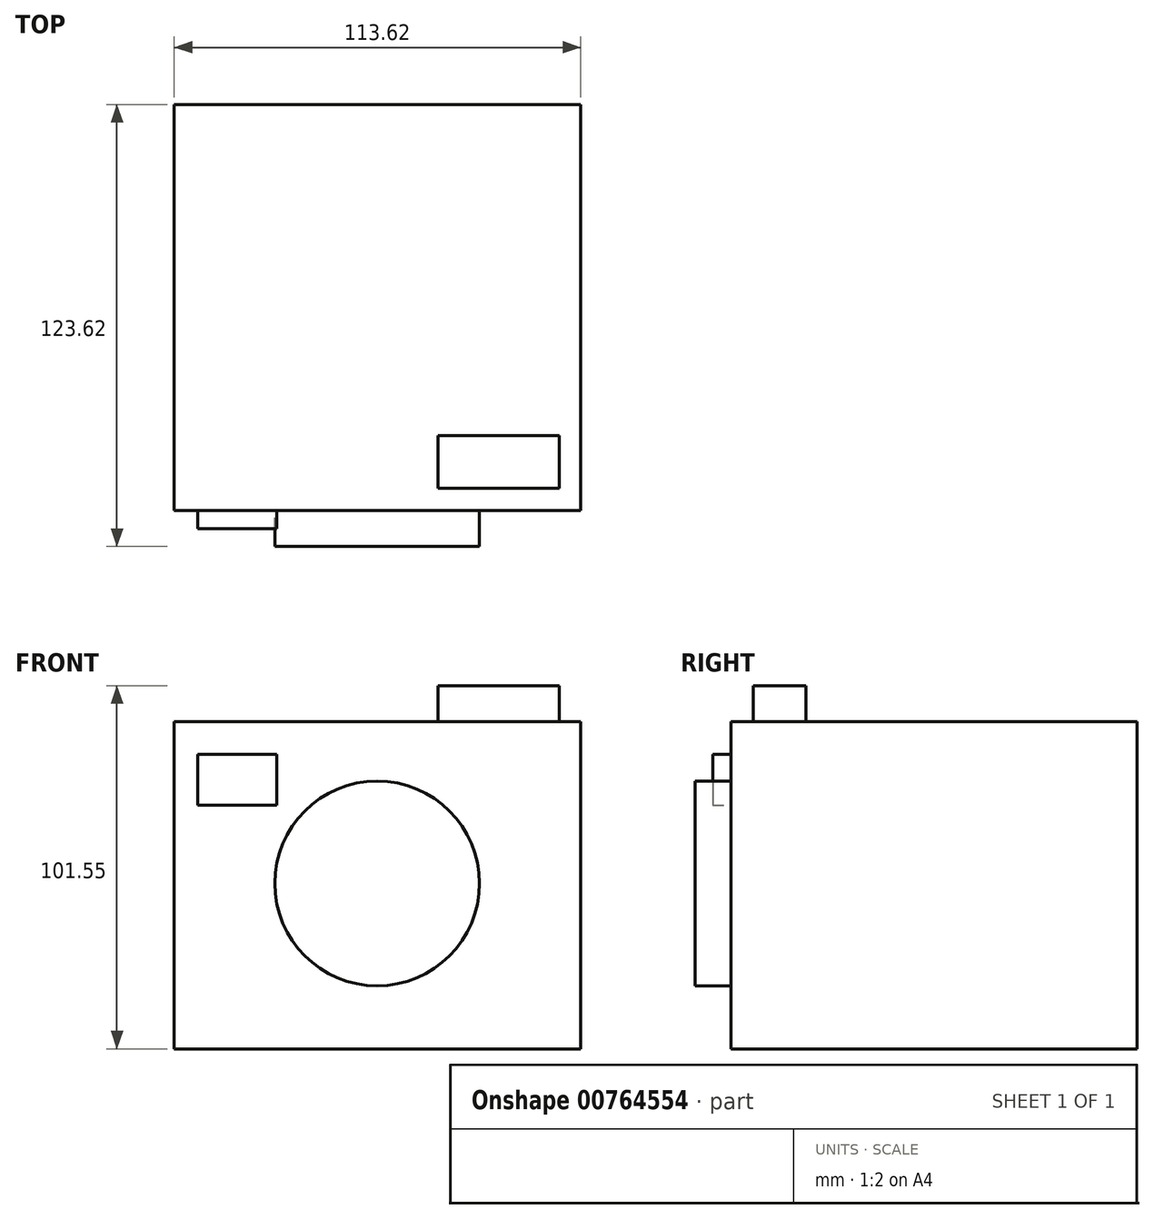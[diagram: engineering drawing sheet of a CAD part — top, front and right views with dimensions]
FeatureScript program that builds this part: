
annotation { "Feature Type Name" : "Feature", "Feature Type Description" : "" }
export const myFeature = defineFeature(function(context is Context, id is Id, definition is map)
    precondition{}
    {
        {
            var Q0;
            Q0=qCreatedBy(makeId("Front.planeOp"),FACE);
            var sketch = newSketch(context, id + "F0", { "sketchPlane" : qUnion([Q0])});
            skLineSegment(sketch, "E0.bottom", {"start": v(-56.7, 45.3) * mm, "end": v(56.91, 45.3) * mm});
            skLineSegment(sketch, "E0.top", {"start": v(-56.7, -46.26) * mm, "end": v(56.91, -46.26) * mm});
            skLineSegment(sketch, "E0.left", {"start": v(-56.7, 45.3) * mm, "end": v(-56.7, -46.26) * mm});
            skLineSegment(sketch, "E0.right", {"start": v(56.91, 45.3) * mm, "end": v(56.91, -46.26) * mm});
            skSolve(sketch);
        }
        {
            var Q0;
            Q0=makeQuery(id+"F0.imprint","IMPRINT",FACE,{"disambiguationData":[TD([[makeQuery(id+"F0.imprint","IMPRINT",EDGE,{"derivedFrom":sQuery(id+"F0.wireOp",EDGE,"E0.bottom")}),-1.0]])]});
            extrude(context, id + "F1", {"entities" : qUnion([Q0]), "depth" : 113.62 * mm, "offsetDistance" : 25.4 * mm});
        }
        {
            var Q0;
            Q0=makeQuery(id+"F1.opExtrude","CAP_FACE",FACE,{"disambiguationData":[OSD([sQuery(id+"F0.wireOp",EDGE,"E0.bottom"),sQuery(id+"F0.wireOp",EDGE,"E0.top"),sQuery(id+"F0.wireOp",EDGE,"E0.left"),sQuery(id+"F0.wireOp",EDGE,"E0.right")])],"isStart":false});
            var sketch = newSketch(context, id + "F2", { "sketchPlane" : qUnion([Q0])});
            skCircle(sketch, "E1", {"center": v(0, 0) * mm, "radius": 28.63 * mm});
            skSolve(sketch);
        }
        {
            var Q0;
            Q0 = qSketchRegion(id + "F2", true);
            extrude(context, id + "F3", {"entities" : qUnion([Q0]), "operationType" : NewBodyOperationType.ADD, "depth" : 10 * mm, "offsetDistance" : 25 * mm});
        }
        {
            var Q0;
            Q0=makeQuery(id+"F3.opExtrude","CAP_FACE",FACE,{"disambiguationData":[OSD([sQuery(id+"F2.wireOp",EDGE,"E1")])],"isStart":false});
            extrude(context, id + "F4", {"entities" : qUnion([Q0]), "operationType" : NewBodyOperationType.ADD, "oppositeDirection" : true, "depth" : 18 * mm, "offsetDistance" : 25 * mm});
        }
        {
            var Q0;
            Q0=makeQuery(id+"F1.opExtrude","CAP_FACE",FACE,{"disambiguationData":[OSD([sQuery(id+"F0.wireOp",EDGE,"E0.bottom"),sQuery(id+"F0.wireOp",EDGE,"E0.top"),sQuery(id+"F0.wireOp",EDGE,"E0.left"),sQuery(id+"F0.wireOp",EDGE,"E0.right")])],"isStart":false});
            var sketch = newSketch(context, id + "F5", { "sketchPlane" : qUnion([Q0])});
            skCircle(sketch, "E2", {"center": v(0, 0) * mm, "radius": 23.26 * mm});
            skSolve(sketch);
        }
        {
            var Q0;
            Q0=sQuery(id+"F5.wireOp",EDGE,"E2");
            extrude(context, id + "F6", {"bodyType" : ToolBodyType.SURFACE, "surfaceEntities" : qUnion([Q0]), "depth" : 20 * mm, "offsetDistance" : 25 * mm});
        }
        {
            var Q0;
            Q0=makeQuery(id+"F1.opExtrude","SWEPT_FACE",FACE,{"disambiguationData":[OSD([sQuery(id+"F0.wireOp",EDGE,"E0.bottom")])]});
            var sketch = newSketch(context, id + "F7", { "sketchPlane" : qUnion([Q0])});
            skLineSegment(sketch, "E3.bottom", {"start": v(17.06, -92.6) * mm, "end": v(50.9, -92.6) * mm});
            skLineSegment(sketch, "E3.top", {"start": v(17.06, -107.4) * mm, "end": v(50.9, -107.4) * mm});
            skLineSegment(sketch, "E3.left", {"start": v(17.06, -92.6) * mm, "end": v(17.06, -107.4) * mm});
            skLineSegment(sketch, "E3.right", {"start": v(50.9, -92.6) * mm, "end": v(50.9, -107.4) * mm});
            skSolve(sketch);
        }
        {
            var Q0;
            Q0 = qSketchRegion(id + "F7", true);
            extrude(context, id + "F8", {"entities" : qUnion([Q0]), "operationType" : NewBodyOperationType.ADD, "depth" : 10 * mm, "offsetDistance" : 25 * mm});
        }
        {
            var Q0;
            Q0=makeQuery(id+"F1.opExtrude","CAP_FACE",FACE,{"disambiguationData":[OSD([sQuery(id+"F0.wireOp",EDGE,"E0.bottom"),sQuery(id+"F0.wireOp",EDGE,"E0.top"),sQuery(id+"F0.wireOp",EDGE,"E0.left"),sQuery(id+"F0.wireOp",EDGE,"E0.right")])],"isStart":false});
            var sketch = newSketch(context, id + "F9", { "sketchPlane" : qUnion([Q0])});
            skLineSegment(sketch, "E4.bottom", {"start": v(-50.17, 36.08) * mm, "end": v(-28.1, 36.08) * mm});
            skLineSegment(sketch, "E4.top", {"start": v(-50.17, 21.93) * mm, "end": v(-28.1, 21.93) * mm});
            skLineSegment(sketch, "E4.left", {"start": v(-50.17, 36.08) * mm, "end": v(-50.17, 21.93) * mm});
            skLineSegment(sketch, "E4.right", {"start": v(-28.1, 36.08) * mm, "end": v(-28.1, 21.93) * mm});
            skSolve(sketch);
        }
        {
            var Q0;
            Q0 = qSketchRegion(id + "F9", true);
            extrude(context, id + "F10", {"entities" : qUnion([Q0]), "operationType" : NewBodyOperationType.ADD, "depth" : 5 * mm, "offsetDistance" : 25 * mm});
        }
        {
            var Q0;
            Q0=makeQuery(id+"F1.opExtrude","CAP_FACE",FACE,{"disambiguationData":[OSD([sQuery(id+"F0.wireOp",EDGE,"E0.bottom"),sQuery(id+"F0.wireOp",EDGE,"E0.top"),sQuery(id+"F0.wireOp",EDGE,"E0.left"),sQuery(id+"F0.wireOp",EDGE,"E0.right")])],"isStart":true});
            var sketch = newSketch(context, id + "F11", { "sketchPlane" : qUnion([Q0])});
            skSolve(sketch);
        }
        {
            var Q0;
            Q0=makeQuery(id+"F11.imprint","IMPRINT",FACE,{"disambiguationData":[TD([[makeQuery(id+"F11.imprint","IMPRINT",EDGE,{"derivedFrom":makeQuery(id+"F1.opExtrude","CAP_EDGE",EDGE,{"disambiguationData":[OSD([sQuery(id+"F0.wireOp",EDGE,"E0.bottom")])],"isStart":true})}),1.0]])]});
            extrude(context, id + "F12", {"entities" : qUnion([Q0]), "operationType" : NewBodyOperationType.ADD, "oppositeDirection" : true, "depth" : 60 * mm, "offsetDistance" : 25 * mm});
        }
    });
